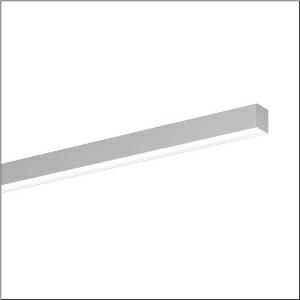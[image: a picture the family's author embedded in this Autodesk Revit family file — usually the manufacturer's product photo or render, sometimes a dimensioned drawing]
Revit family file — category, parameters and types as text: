
# Revit family: silica_r__21_51mx23db35sb_5652
name_source: partatom
category: Lighting Fixtures
units: mm (PartAtom-declared; Revit-internal decimal feet)

## family parameters
Cut with Voids When Loaded = No
Host = Face
Light Source = No
Part Type = Normal
Room Calculation Point = No
Round Connector Dimension = Use Diameter
Shared = No

## types (1)
- --- (1 x LED, 4100 lm, 30.1 W, 3000K)
    Apparent Load = 30 VA
    CIE Flux Codes = 78 96 99 100 100
    Color Rendering = 80
    Color Temperature = 3000K
    Default Elevation = 1800 mm
    Description = Silica® 21, office luminaire, primary optical cover: prismatic diffuser, of PMMA, CAT 2 (L<= 3000cd/m²), light emission: direct distribution, primary light characteristic: symmetric, installation type: surface-mounted, LED, rated luminous flux: 4.100lm, luminous efficacy: 136lm/W, light colour: 830, colour temperature: 3000K, control gear: DALI 2, with terminal, 3+2-pole, max. 2.5mm², mains connection: 220..240V, AC, 50/60Hz, rated input power: 30.1W, luminaire housing, of aluminium, metallic grey (RAL 9006), length: 1.504mm, width: 53mm, height: 53mm, protection rating (complete): IP20, insulation class (complete): insulation class I (protective earthing), certification: CE, permissible operating ambient temperature: 0..+35°C, standard: EN 50419, packaging unit: 1 piece
    Height = 53 mm
    Lamp = 1 x LED
    Lamp Light Flux = 4100 lm
    Lamp Power = 30.1 W
    Lamp count = 1
    Length = 1504 mm
    Luminous efficacy = 136 lm/W
    Manufacturer = Siteco
    ModVariant = No
    Model = 51MX23DB35SB
    Mounting Place = Ceiling
    Mounting Type = Surface mounted
    Number of Poles = 1
    OnlyDefault = Yes
    Power Factor = 1
    Product Name = Silica® 21
    Product group = office luminaire | ceiling mounted
    ProductGroupID = 302
    Protection Class = Protection class I
    Protection Degree = IP 20
    RLX_Detail_Level = 1
    RLX_Emergency_Light_Flux = 0 lm
    RLX_Emergency_Type = 0
    RLX_Emergency_Type_DB = No
    RlxData = <blob elided: 21309 chars, md5=9d23c14e>
    Socket = socket
    Standby Power = 0 W
    System Light Flux = 4100 lm
    System Power = 30 W
    Type Comments = factory setting: luminous flux: 100 % | dim-lin: 254 | 345 mA
    Type Image = l_1335933.jpg
    URL = http://relux.com
    VarID = @adj_119212
    Voltage = 0 V
    Weight = 0.00 kg
    Width = 53 mm

## geometry (parser evidence)
native form markers: Blend x4, Sweep x10
no freeform markers — native parametric forms only
